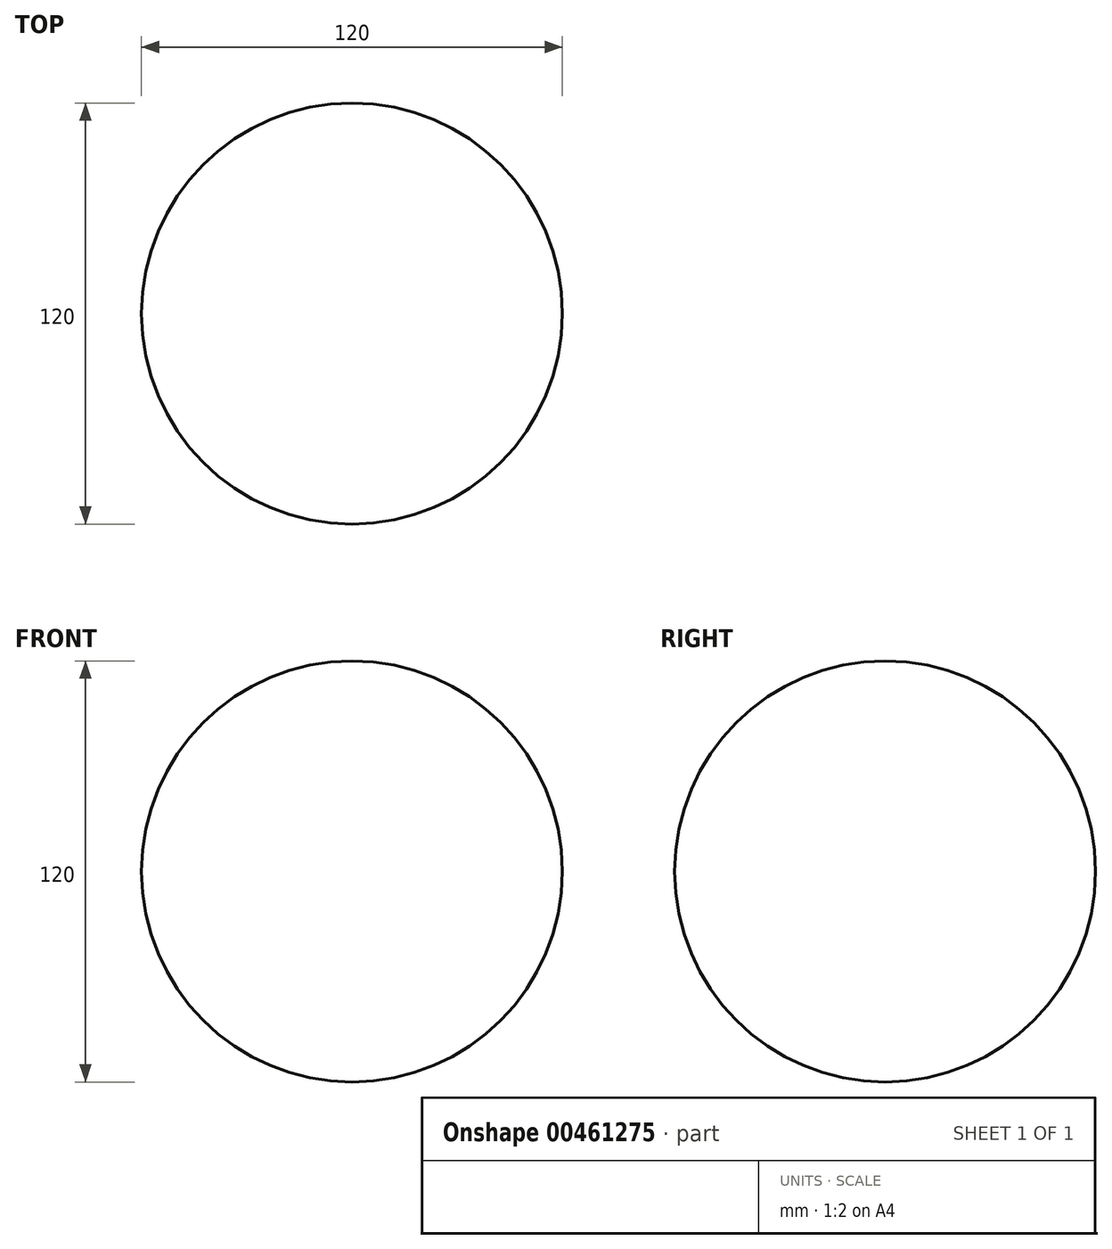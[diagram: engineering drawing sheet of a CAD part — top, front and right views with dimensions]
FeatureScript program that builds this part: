
annotation { "Feature Type Name" : "Feature", "Feature Type Description" : "" }
export const myFeature = defineFeature(function(context is Context, id is Id, definition is map)
    precondition{}
    {
        {
            var Q0;
            Q0=qCreatedBy(makeId("Top.planeOp"),FACE);
            var sketch = newSketch(context, id + "F0", { "sketchPlane" : qUnion([Q0])});
            skArc(sketch, "E0", {"start": v(0, 60) * mm, "mid": v(-60, 0) * mm, "end": v(0, -60) * mm});
            skLineSegment(sketch, "E1", {"start": v(0, 68.25) * mm, "end": v(0, -72.43) * mm});
            skSolve(sketch);
        }
        {
            var Q0;
            Q0 = qSketchRegion(id + "F0", true);
            var Q1;
            Q1=sQuery(id+"F0.wireOp",EDGE,"E1");
            revolve(context, id + "F1", {"entities" : qUnion([Q0]), "axis" : qUnion([Q1]), "revolveType" : RevolveType.FULL});
        }
    });
